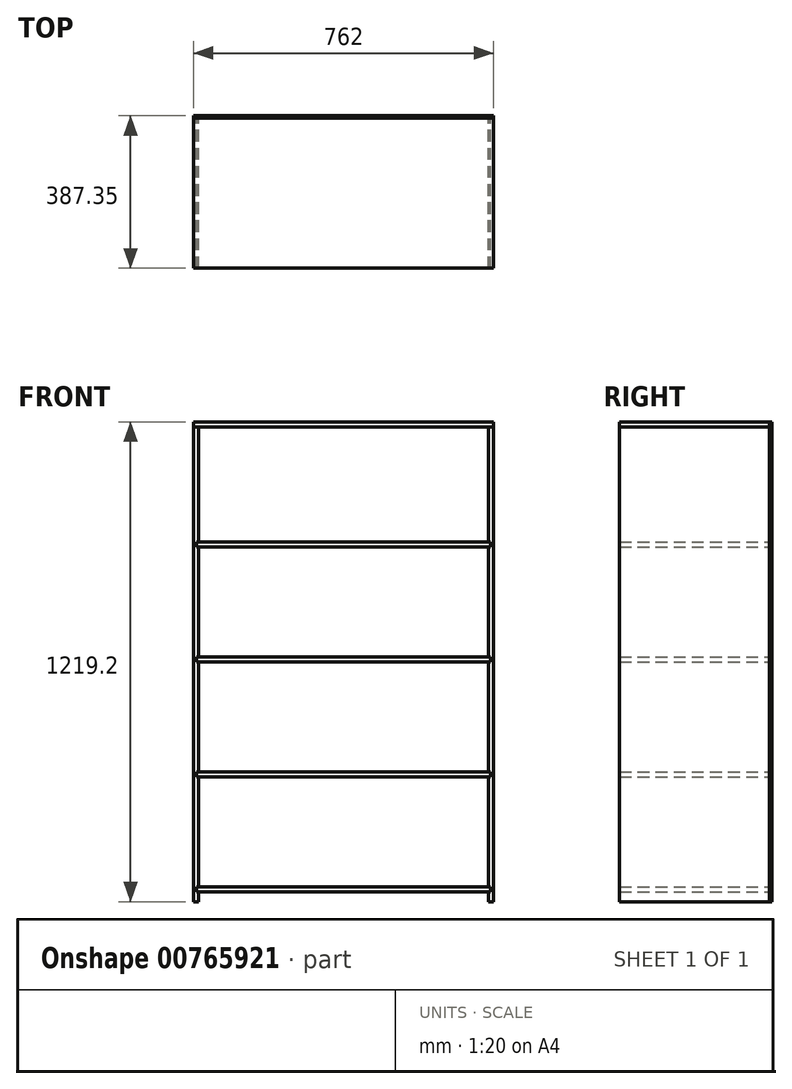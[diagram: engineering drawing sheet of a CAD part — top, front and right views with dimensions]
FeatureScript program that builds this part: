
annotation { "Feature Type Name" : "Feature", "Feature Type Description" : "" }
export const myFeature = defineFeature(function(context is Context, id is Id, definition is map)
    precondition{}
    {
        {
            var Q0;
            Q0=qCreatedBy(makeId("Front.planeOp"),FACE);
            var sketch = newSketch(context, id + "F0", { "sketchPlane" : qUnion([Q0])});
            skLineSegment(sketch, "E0.bottom", {"start": v(0, 0) * mm, "end": v(12.7, 0) * mm});
            skLineSegment(sketch, "E0.top", {"start": v(0, 1219.2) * mm, "end": v(762, 1219.2) * mm});
            skLineSegment(sketch, "E0.left", {"start": v(0, 0) * mm, "end": v(0, 1219.2) * mm});
            skLineSegment(sketch, "E0.right", {"start": v(12.7, 0) * mm, "end": v(12.7, 25.4) * mm});
            skLineSegment(sketch, "E1.top", {"start": v(0, 1206.5) * mm, "end": v(762, 1206.5) * mm});
            skLineSegment(sketch, "E2.top", {"start": v(749.3, 0) * mm, "end": v(762, 0) * mm});
            skLineSegment(sketch, "E2.left", {"start": v(749.3, 1206.5) * mm, "end": v(749.3, 914.4) * mm});
            skLineSegment(sketch, "E2.right", {"start": v(762, 1219.2) * mm, "end": v(762, 0) * mm});
            skLineSegment(sketch, "E3.bottom", {"start": v(7.94, 25.4) * mm, "end": v(754.06, 25.4) * mm});
            skLineSegment(sketch, "E3.top", {"start": v(7.94, 38.1) * mm, "end": v(754.06, 38.1) * mm});
            skLineSegment(sketch, "E4.0", {"start": v(754.06, 38.1) * mm, "end": v(754.06, 25.4) * mm});
            skLineSegment(sketch, "E5.trimOffspring", {"start": v(749.3, 25.4) * mm, "end": v(749.3, 0) * mm});
            skLineSegment(sketch, "E6.0", {"start": v(7.94, 25.4) * mm, "end": v(7.94, 38.1) * mm});
            skLineSegment(sketch, "E7.trimOffspring", {"start": v(12.7, 38.1) * mm, "end": v(12.7, 317.5) * mm});
            skLineSegment(sketch, "E8.0.1.0", {"start": v(7.94, 317.5) * mm, "end": v(754.06, 317.5) * mm});
            skLineSegment(sketch, "E8.0.1.1", {"start": v(7.94, 330.2) * mm, "end": v(754.06, 330.2) * mm});
            skLineSegment(sketch, "E8.0.2.0", {"start": v(7.94, 609.6) * mm, "end": v(754.06, 609.6) * mm});
            skLineSegment(sketch, "E8.0.2.1", {"start": v(7.94, 622.3) * mm, "end": v(754.06, 622.3) * mm});
            skLineSegment(sketch, "E8.0.3.0", {"start": v(7.94, 901.7) * mm, "end": v(754.06, 901.7) * mm});
            skLineSegment(sketch, "E8.0.3.1", {"start": v(7.94, 914.4) * mm, "end": v(754.06, 914.4) * mm});
            skLineSegment(sketch, "E8.direction1", {"start": v(7.94, 25.4) * mm, "end": v(33.34, 25.4) * mm, "construction": true});
            skLineSegment(sketch, "E8.direction2", {"start": v(7.94, 25.4) * mm, "end": v(7.94, 317.5) * mm, "construction": true});
            skLineSegment(sketch, "E9", {"start": v(754.06, 330.2) * mm, "end": v(754.06, 317.5) * mm});
            skLineSegment(sketch, "E10.trimOffspring", {"start": v(749.3, 317.5) * mm, "end": v(749.3, 38.1) * mm});
            skLineSegment(sketch, "E11", {"start": v(7.94, 622.3) * mm, "end": v(7.94, 609.6) * mm});
            skLineSegment(sketch, "E12", {"start": v(754.06, 622.3) * mm, "end": v(754.06, 609.6) * mm});
            skLineSegment(sketch, "E13", {"start": v(749.3, 609.6) * mm, "end": v(749.3, 330.2) * mm});
            skLineSegment(sketch, "E14.trimOffspring", {"start": v(749.3, 901.7) * mm, "end": v(749.3, 622.3) * mm});
            skLineSegment(sketch, "E15.trimOffspring", {"start": v(12.7, 914.4) * mm, "end": v(12.7, 1206.5) * mm});
            skLineSegment(sketch, "E16", {"start": v(754.06, 914.4) * mm, "end": v(754.06, 901.7) * mm});
            skLineSegment(sketch, "E17", {"start": v(7.94, 914.4) * mm, "end": v(7.94, 901.7) * mm});
            skLineSegment(sketch, "E18.trimOffspring", {"start": v(12.7, 622.3) * mm, "end": v(12.7, 901.7) * mm});
            skLineSegment(sketch, "E19.trimOffspring", {"start": v(12.7, 330.2) * mm, "end": v(12.7, 609.6) * mm});
            skLineSegment(sketch, "E20", {"start": v(7.94, 330.2) * mm, "end": v(7.94, 317.5) * mm});
            skLineSegment(sketch, "E21", {"start": v(7.94, 38.1) * mm, "end": v(7.94, 25.4) * mm});
            skSolve(sketch);
        }
        {
            var Q0;
            {var subQ15=sQuery(id+"F0.wireOp",EDGE,"E2.top");Q0=makeQuery(id+"F0.imprint","IMPRINT",FACE,{"disambiguationData":[TD([[makeQuery(id+"F0.imprint","IMPRINT",EDGE,{"derivedFrom":subQ15}),1.0]])]});}
            var Q1;
            {var subQ6=sQuery(id+"F0.wireOp",EDGE,"E0.bottom");Q1=makeQuery(id+"F0.imprint","IMPRINT",FACE,{"disambiguationData":[TD([[makeQuery(id+"F0.imprint","IMPRINT",EDGE,{"derivedFrom":subQ6}),1.0]])]});}
            extrude(context, id + "F1", {"entities" : qUnion([Q0, Q1]), "depth" : 381 * mm, "offsetDistance" : 25.4 * mm});
        }
        {
            var Q0;
            {var subQ3=sQuery(id+"F0.wireOp",EDGE,"E4.0");Q0=makeQuery(id+"F0.imprint","IMPRINT",FACE,{"disambiguationData":[TD([[makeQuery(id+"F0.imprint","IMPRINT",EDGE,{"derivedFrom":subQ3}),-1.0]])]});}
            var Q1;
            {var subQ3=sQuery(id+"F0.wireOp",EDGE,"E9");Q1=makeQuery(id+"F0.imprint","IMPRINT",FACE,{"disambiguationData":[TD([[makeQuery(id+"F0.imprint","IMPRINT",EDGE,{"derivedFrom":subQ3}),-1.0]])]});}
            var Q2;
            {var subQ0=sQuery(id+"F0.wireOp",EDGE,"E11");Q2=makeQuery(id+"F0.imprint","IMPRINT",FACE,{"disambiguationData":[TD([[makeQuery(id+"F0.imprint","IMPRINT",EDGE,{"derivedFrom":subQ0}),1.0]])]});}
            var Q3;
            {var subQ3=sQuery(id+"F0.wireOp",EDGE,"E16");Q3=makeQuery(id+"F0.imprint","IMPRINT",FACE,{"disambiguationData":[TD([[makeQuery(id+"F0.imprint","IMPRINT",EDGE,{"derivedFrom":subQ3}),-1.0]])]});}
            var Q4;
            {var subQ4=sQuery(id+"F0.wireOp",EDGE,"E0.top");Q4=makeQuery(id+"F0.imprint","IMPRINT",FACE,{"disambiguationData":[TD([[makeQuery(id+"F0.imprint","IMPRINT",EDGE,{"derivedFrom":subQ4}),-1.0]])]});}
            extrude(context, id + "F2", {"entities" : qUnion([Q0, Q1, Q2, Q3, Q4]), "depth" : 381 * mm, "offsetDistance" : 25.4 * mm});
        }
        {
            var Q0;
            {var subQ0=sQuery(id+"F0.wireOp",EDGE,"E2.left");Q0=makeQuery(id+"F0.imprint","IMPRINT",FACE,{"disambiguationData":[TD([[makeQuery(id+"F0.imprint","IMPRINT",EDGE,{"derivedFrom":subQ0}),-1.0]])]});}
            var Q1;
            {var subQ0=sQuery(id+"F0.wireOp",EDGE,"E14.trimOffspring");Q1=makeQuery(id+"F0.imprint","IMPRINT",FACE,{"disambiguationData":[TD([[makeQuery(id+"F0.imprint","IMPRINT",EDGE,{"derivedFrom":subQ0}),-1.0]])]});}
            var Q2;
            {var subQ0=sQuery(id+"F0.wireOp",EDGE,"E13");Q2=makeQuery(id+"F0.imprint","IMPRINT",FACE,{"disambiguationData":[TD([[makeQuery(id+"F0.imprint","IMPRINT",EDGE,{"derivedFrom":subQ0}),-1.0]])]});}
            var Q3;
            {var subQ0=sQuery(id+"F0.wireOp",EDGE,"E7.trimOffspring");Q3=makeQuery(id+"F0.imprint","IMPRINT",FACE,{"disambiguationData":[TD([[makeQuery(id+"F0.imprint","IMPRINT",EDGE,{"derivedFrom":subQ0}),-1.0]])]});}
            var Q4;
            {var subQ15=sQuery(id+"F0.wireOp",EDGE,"E2.top");Q4=makeQuery(id+"F0.imprint","IMPRINT",FACE,{"disambiguationData":[TD([[makeQuery(id+"F0.imprint","IMPRINT",EDGE,{"derivedFrom":subQ15}),1.0]])]});}
            var Q5;
            {var subQ6=sQuery(id+"F0.wireOp",EDGE,"E0.bottom");Q5=makeQuery(id+"F0.imprint","IMPRINT",FACE,{"disambiguationData":[TD([[makeQuery(id+"F0.imprint","IMPRINT",EDGE,{"derivedFrom":subQ6}),1.0]])]});}
            var Q6;
            {var subQ4=sQuery(id+"F0.wireOp",EDGE,"E0.top");Q6=makeQuery(id+"F0.imprint","IMPRINT",FACE,{"disambiguationData":[TD([[makeQuery(id+"F0.imprint","IMPRINT",EDGE,{"derivedFrom":subQ4}),-1.0]])]});}
            var Q7;
            {var subQ3=sQuery(id+"F0.wireOp",EDGE,"E16");Q7=makeQuery(id+"F0.imprint","IMPRINT",FACE,{"disambiguationData":[TD([[makeQuery(id+"F0.imprint","IMPRINT",EDGE,{"derivedFrom":subQ3}),-1.0]])]});}
            var Q8;
            {var subQ0=sQuery(id+"F0.wireOp",EDGE,"E11");Q8=makeQuery(id+"F0.imprint","IMPRINT",FACE,{"disambiguationData":[TD([[makeQuery(id+"F0.imprint","IMPRINT",EDGE,{"derivedFrom":subQ0}),1.0]])]});}
            var Q9;
            {var subQ3=sQuery(id+"F0.wireOp",EDGE,"E9");Q9=makeQuery(id+"F0.imprint","IMPRINT",FACE,{"disambiguationData":[TD([[makeQuery(id+"F0.imprint","IMPRINT",EDGE,{"derivedFrom":subQ3}),-1.0]])]});}
            var Q10;
            {var subQ3=sQuery(id+"F0.wireOp",EDGE,"E4.0");Q10=makeQuery(id+"F0.imprint","IMPRINT",FACE,{"disambiguationData":[TD([[makeQuery(id+"F0.imprint","IMPRINT",EDGE,{"derivedFrom":subQ3}),-1.0]])]});}
            extrude(context, id + "F3", {"entities" : qUnion([Q0, Q1, Q2, Q3, Q4, Q5, Q6, Q7, Q8, Q9, Q10]), "oppositeDirection" : true, "depth" : 6.35 * mm, "offsetDistance" : 25.4 * mm});
        }
    });
